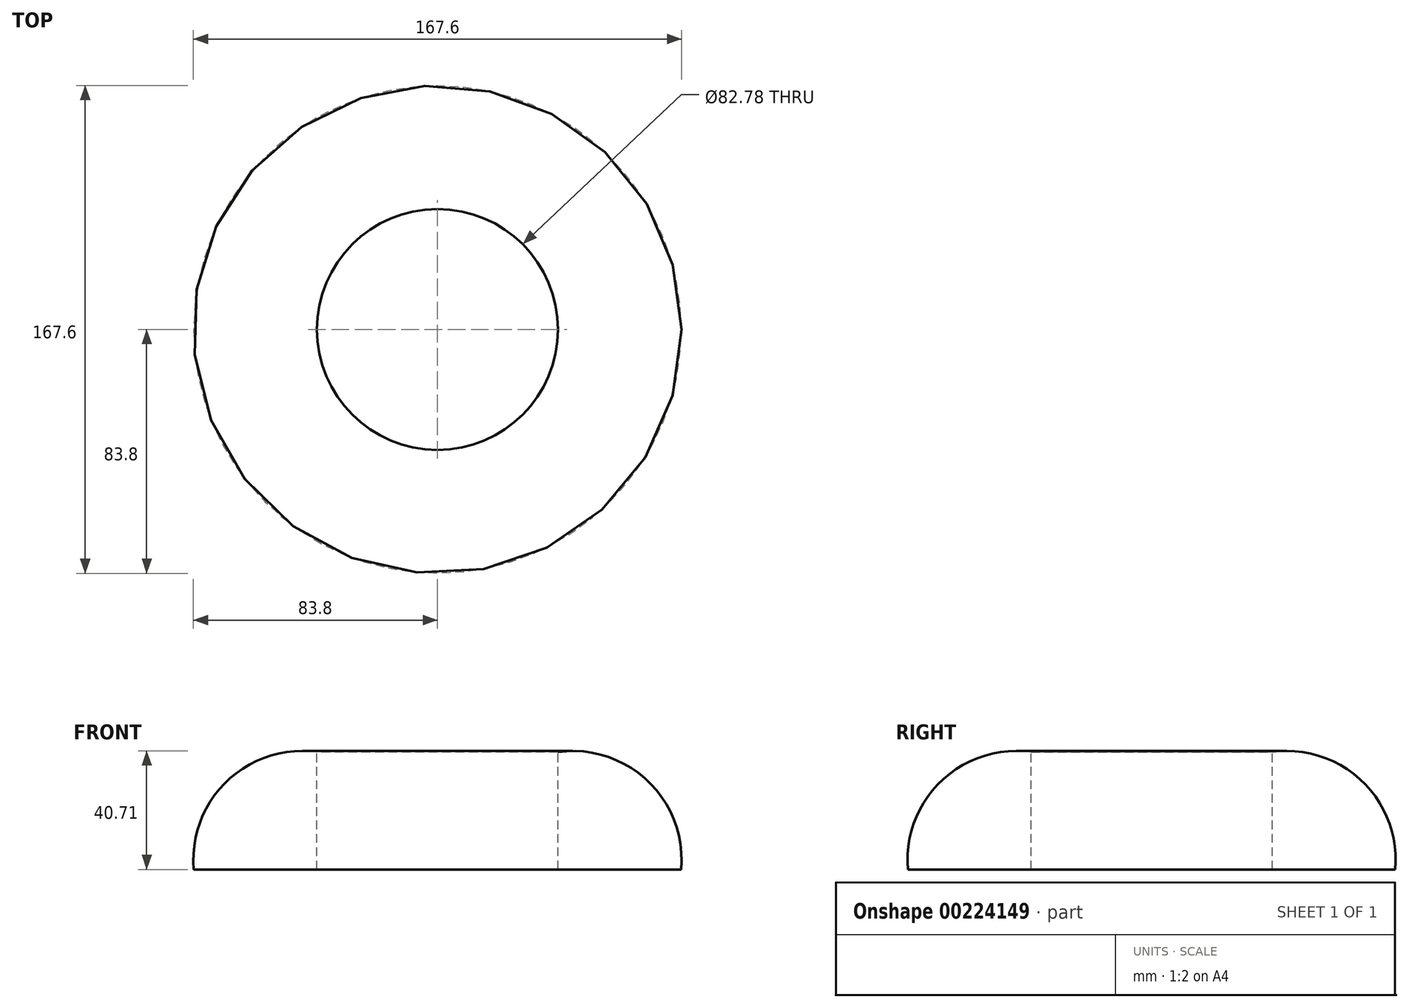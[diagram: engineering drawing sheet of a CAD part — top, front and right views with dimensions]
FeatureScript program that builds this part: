
annotation { "Feature Type Name" : "Feature", "Feature Type Description" : "" }
export const myFeature = defineFeature(function(context is Context, id is Id, definition is map)
    precondition{}
    {
        {
            var Q0;
            Q0=qCreatedBy(makeId("Front.planeOp"),FACE);
            var sketch = newSketch(context, id + "F0", { "sketchPlane" : qUnion([Q0])});
            skLineSegment(sketch, "E0", {"start": v(0, 0) * mm, "end": v(0, 40.37) * mm});
            skArc(sketch, "E1", {"start": v(42.26, 0) * mm, "mid": v(30.86, 30.37) * mm, "end": v(0, 40.37) * mm});
            skLineSegment(sketch, "E2", {"start": v(0, 0) * mm, "end": v(42.26, 0) * mm});
            skSolve(sketch);
        }
        {
            var Q0;
            Q0=qCreatedBy(makeId("Front.planeOp"),FACE);
            var sketch = newSketch(context, id + "F1", { "sketchPlane" : qUnion([Q0])});
            skLineSegment(sketch, "E3", {"start": v(-41.39, 40.08) * mm, "end": v(-41.39, -26.96) * mm});
            skSolve(sketch);
        }
        {
            var Q0;
            Q0=makeQuery(id+"F0.imprint","IMPRINT",FACE,{"disambiguationData":[TD([[makeQuery(id+"F0.imprint","IMPRINT",EDGE,{"derivedFrom":sQuery(id+"F0.wireOp",EDGE,"E0")}),-1.0]])]});
            var Q1;
            Q1=sQuery(id+"F1.wireOp",EDGE,"E3");
            revolve(context, id + "F2", {"entities" : qUnion([Q0]), "axis" : qUnion([Q1]), "revolveType" : RevolveType.FULL});
        }
    });
